# Revit family: Midea_VRF_Indoor_MI2-560FADHN1(50Hz-60Hz)
name_source: partatom
category: Equipamento mecânico
units: mm (PartAtom-declared; Revit-internal decimal feet)

## family parameters
Com base no plano de trabalho = Não
Compartilhado = Não
Corte com vazios quando carregada = Não
Cota do conector redondo = Utilizar diâmetro
Número OmniClass = 23.75.00.00
Ponto de cálculo do ambiente = Não
Sempre na vertical = Sim
Tipo de parte = Normal
Título OmniClass = Climate Control (HVAC)

## types (1)
- 4TVF0192EF000AA
    Air  Flow = 6000/5665/5330/5000/4665/4330/4000 m3/h
    Condensation = air
    Cooling Capacity = 56.00 kW
    Cooling Power Input = 2272.000 W
    Depth = 905  [stored 2.96916 ft]
    Descrição = High efficiency air cooled
    Fabricante = TRANE
    Gas = R410a
    Gas pipe = 28.6
    Heating Capacity = 39.00 kW
    Heating Power Input = 2272.000 W
    Height = 680  [stored 2.23097 ft]
    Installation = Indoor installation
    Liquid pipe = 15.9  [stored 0.0521654 ft]
    Maximum Fuse Amps = 30 A
    Minimum Circuit Amps = 15 A
    Modelo = 4TVF0192EF000AA
    Net Weight = 218.00 kg
    Power supply = 220-240V ~50/60Hz
    Series = ULTRA
    URL = https://www.trane.com
    Width = 2010  [stored 6.59449 ft]
    clearance access behind = 600  [stored 1.9685 ft]
    clearance access front = 500  [stored 1.64042 ft]
    clearance access left = 600  [stored 1.9685 ft]
    clearance access right = 600  [stored 1.9685 ft]

note: [stored X ft] marks values corroborated as IEEE doubles in the binary element streams (Revit-internal decimal feet)

## geometry (parser evidence)
native form markers: Blend x2, Sweep x8
no freeform markers — native parametric forms only
